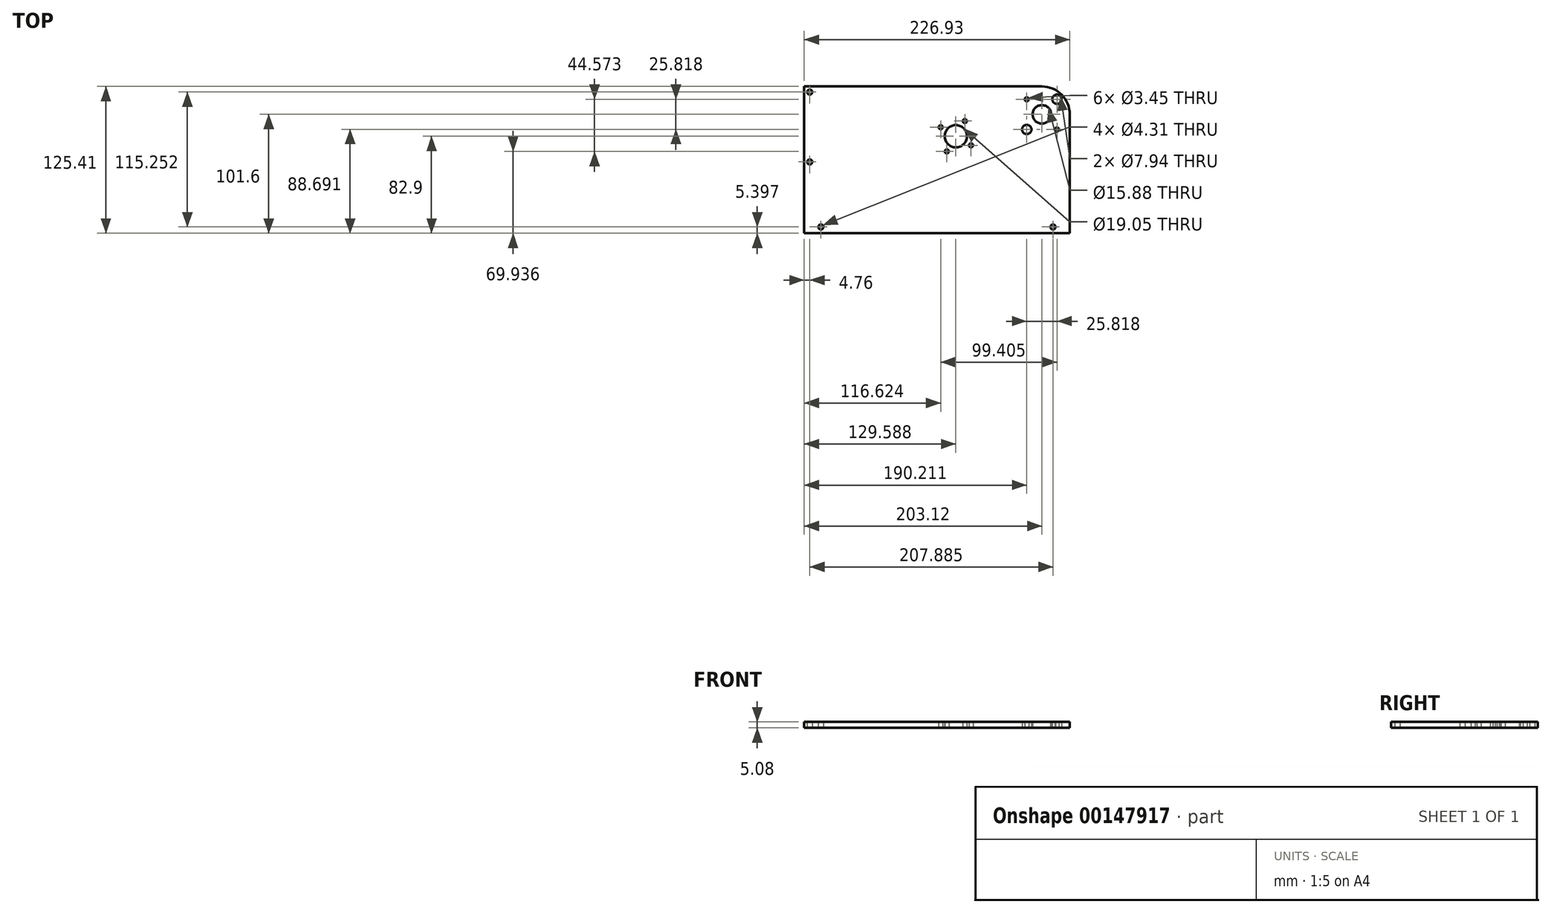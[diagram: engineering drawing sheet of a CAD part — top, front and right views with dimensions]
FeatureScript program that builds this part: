
annotation { "Feature Type Name" : "Feature", "Feature Type Description" : "" }
export const myFeature = defineFeature(function(context is Context, id is Id, definition is map)
    precondition{}
    {
        {
            var Q0;
            Q0=qCreatedBy(makeId("Top.planeOp"),FACE);
            var sketch = newSketch(context, id + "F0", { "sketchPlane" : qUnion([Q0])});
            skCircle(sketch, "E0", {"center": v(0, 0) * mm, "radius": 7.94 * mm});
            skCircle(sketch, "E1", {"center": v(-12.9, 12.9) * mm, "radius": 5.56 * mm, "construction": true});
            skCircle(sketch, "E2", {"center": v(-12.9, 12.9) * mm, "radius": 1.73 * mm});
            skCircle(sketch, "E3", {"center": v(12.9, -12.9) * mm, "radius": 1.73 * mm});
            skLineSegment(sketch, "E4.bottom", {"start": v(-193.6, 23.81) * mm, "end": v(0, 23.81) * mm});
            skLineSegment(sketch, "E4.top", {"start": v(-203.12, -101.6) * mm, "end": v(23.81, -101.6) * mm});
            skLineSegment(sketch, "E4.left", {"start": v(-203.12, 23.81) * mm, "end": v(-203.12, -101.6) * mm});
            skLineSegment(sketch, "E5.bottom", {"start": v(-12.9, 12.9) * mm, "end": v(12.9, 12.9) * mm, "construction": true});
            skLineSegment(sketch, "E5.top", {"start": v(-12.9, -12.9) * mm, "end": v(12.9, -12.9) * mm, "construction": true});
            skLineSegment(sketch, "E5.left", {"start": v(-12.9, 12.9) * mm, "end": v(-12.9, -12.9) * mm, "construction": true});
            skLineSegment(sketch, "E5.right", {"start": v(12.9, 12.9) * mm, "end": v(12.9, -12.9) * mm, "construction": true});
            skCircle(sketch, "E6", {"center": v(-12.9, -12.9) * mm, "radius": 3.97 * mm});
            skCircle(sketch, "E7", {"center": v(12.9, 12.9) * mm, "radius": 3.97 * mm});
            skArc(sketch, "E8", {"start": v(23.81, 0) * mm, "mid": v(16.84, 16.84) * mm, "end": v(0, 23.81) * mm});
            skLineSegment(sketch, "E9", {"start": v(23.81, -101.6) * mm, "end": v(23.81, -90.8) * mm});
            skLineSegment(sketch, "E10", {"start": v(23.81, -90.8) * mm, "end": v(23.81, 0) * mm});
            skLineSegment(sketch, "E11", {"start": v(0, 0) * mm, "end": v(0, -101.6) * mm, "construction": true});
            skLineSegment(sketch, "E12", {"start": v(23.81, -96.2) * mm, "end": v(9.53, -96.2) * mm, "construction": true});
            skCircle(sketch, "E13", {"center": v(9.53, -96.2) * mm, "radius": 2.15 * mm});
            skLineSegment(sketch, "E14", {"start": v(23.81, -90.8) * mm, "end": v(0, -90.8) * mm, "construction": true});
            skLineSegment(sketch, "E15", {"start": v(-203.12, 23.81) * mm, "end": v(-193.6, 23.81) * mm});
            skLineSegment(sketch, "E16", {"start": v(-198.36, 23.81) * mm, "end": v(-198.36, 19.05) * mm, "construction": true});
            skLineSegment(sketch, "E17", {"start": v(-203.12, -96.2) * mm, "end": v(-188.83, -96.2) * mm, "construction": true});
            skCircle(sketch, "E18", {"center": v(-188.83, -96.2) * mm, "radius": 2.15 * mm});
            skCircle(sketch, "E19", {"center": v(-198.36, 19.05) * mm, "radius": 2.15 * mm});
            skLineSegment(sketch, "E20", {"start": v(0, 0) * mm, "end": v(-198.36, 0) * mm, "construction": true});
            skLineSegment(sketch, "E21", {"start": v(-198.36, 0) * mm, "end": v(-198.36, 19.05) * mm, "construction": true});
            skLineSegment(sketch, "E22", {"start": v(-198.36, 0) * mm, "end": v(-198.36, -40.65) * mm, "construction": true});
            skLineSegment(sketch, "E23", {"start": v(-198.36, -40.65) * mm, "end": v(-198.36, -96.2) * mm, "construction": true});
            skCircle(sketch, "E24", {"center": v(-198.36, -40.65) * mm, "radius": 2.15 * mm});
            skLineSegment(sketch, "E25", {"start": v(0, 0) * mm, "end": v(-73.53, -18.7) * mm, "construction": true});
            skLineSegment(sketch, "E26.bottom", {"start": v(-86.5, -11) * mm, "end": v(-65.83, -5.74) * mm, "construction": true});
            skLineSegment(sketch, "E26.top", {"start": v(-81.24, -31.66) * mm, "end": v(-60.57, -26.4) * mm, "construction": true});
            skLineSegment(sketch, "E26.left", {"start": v(-86.5, -11) * mm, "end": v(-81.24, -31.66) * mm, "construction": true});
            skLineSegment(sketch, "E26.right", {"start": v(-65.83, -5.74) * mm, "end": v(-60.57, -26.4) * mm, "construction": true});
            skPoint(sketch, "E26.middle", {"position": v(-73.53, -18.7) * mm});
            skCircle(sketch, "E27", {"center": v(-86.5, -11) * mm, "radius": 1.73 * mm});
            skCircle(sketch, "E28", {"center": v(-65.83, -5.74) * mm, "radius": 1.73 * mm});
            skCircle(sketch, "E29", {"center": v(-73.53, -18.7) * mm, "radius": 9.53 * mm});
            skCircle(sketch, "E30", {"center": v(-81.24, -31.66) * mm, "radius": 1.73 * mm});
            skCircle(sketch, "E31", {"center": v(-60.57, -26.4) * mm, "radius": 1.73 * mm});
            skCircle(sketch, "E32", {"center": v(-73.53, -18.7) * mm, "radius": 11.11 * mm, "construction": true});
            skCircle(sketch, "E33", {"center": v(-81.24, -31.66) * mm, "radius": 3.97 * mm, "construction": true});
            skSolve(sketch);
        }
        {
            var Q0;
            Q0=qSketchRegion(id+"F0",true);
            extrude(context, id + "F1", {"entities" : qUnion([Q0]), "depth" : 5.08 * mm});
        }
    });
